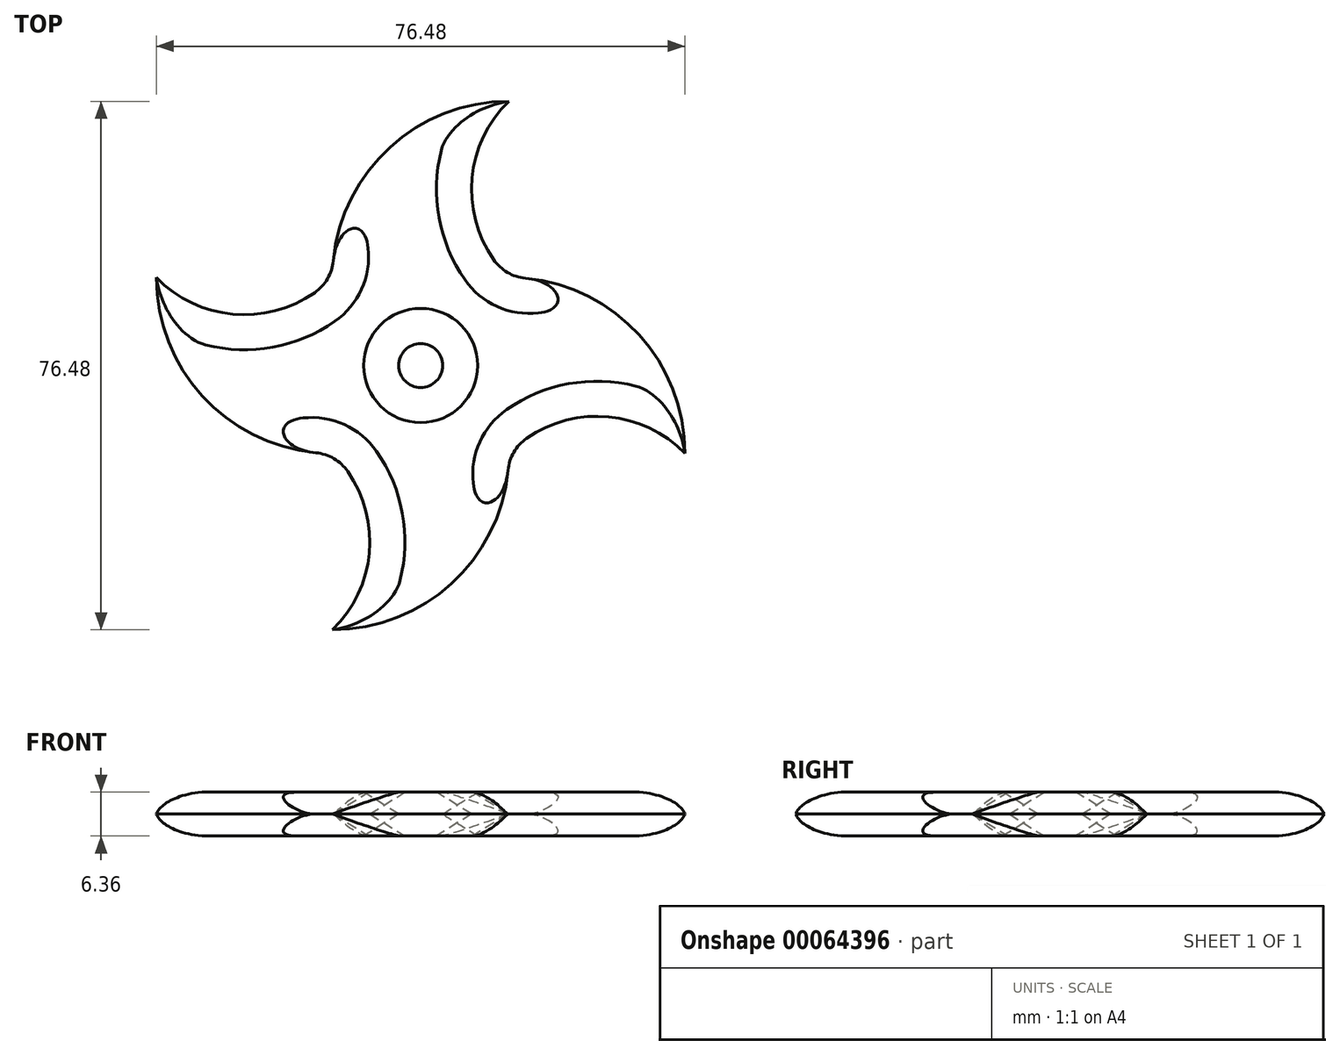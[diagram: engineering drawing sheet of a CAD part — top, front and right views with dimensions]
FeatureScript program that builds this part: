
annotation { "Feature Type Name" : "Feature", "Feature Type Description" : "" }
export const myFeature = defineFeature(function(context is Context, id is Id, definition is map)
    precondition{}
    {
        {
            var Q0;
            Q0=qCreatedBy(makeId("Top.planeOp"),FACE);
            var sketch = newSketch(context, id + "F0", { "sketchPlane" : qUnion([Q0])});
            skLineSegment(sketch, "E0.bottom", {"start": v(-12.75, 12.75) * mm, "end": v(12.74, 12.75) * mm});
            skLineSegment(sketch, "E0.top", {"start": v(-12.75, -12.74) * mm, "end": v(12.74, -12.74) * mm});
            skLineSegment(sketch, "E0.left", {"start": v(-12.75, 12.75) * mm, "end": v(-12.75, -12.74) * mm});
            skLineSegment(sketch, "E0.right", {"start": v(12.74, 12.75) * mm, "end": v(12.74, -12.74) * mm});
            skArc(sketch, "E1", {"start": v(-12.64, 15.16) * mm, "mid": v(-4.41, 31.6) * mm, "end": v(12.74, 38.24) * mm});
            skArc(sketch, "E2", {"start": v(12.74, 38.24) * mm, "mid": v(7.44, 27.18) * mm, "end": v(10.55, 15.33) * mm});
            skCircle(sketch, "E3", {"center": v(0, 0) * mm, "radius": 3.18 * mm});
            skArc(sketch, "E4.1.0", {"start": v(-38.24, 12.74) * mm, "mid": v(-27.18, 7.44) * mm, "end": v(-15.33, 10.55) * mm});
            skArc(sketch, "E4.1.1", {"start": v(-15.16, -12.64) * mm, "mid": v(-31.6, -4.41) * mm, "end": v(-38.24, 12.74) * mm});
            skLineSegment(sketch, "E4.1.2", {"start": v(-12.75, -12.75) * mm, "end": v(-12.75, 12.74) * mm});
            skArc(sketch, "E4.2.0", {"start": v(-12.74, -38.24) * mm, "mid": v(-7.44, -27.18) * mm, "end": v(-10.55, -15.33) * mm});
            skArc(sketch, "E4.2.1", {"start": v(12.64, -15.16) * mm, "mid": v(4.41, -31.6) * mm, "end": v(-12.74, -38.24) * mm});
            skLineSegment(sketch, "E4.2.2", {"start": v(12.75, -12.75) * mm, "end": v(-12.74, -12.75) * mm});
            skArc(sketch, "E4.3.0", {"start": v(38.24, -12.74) * mm, "mid": v(27.18, -7.44) * mm, "end": v(15.33, -10.55) * mm});
            skArc(sketch, "E4.3.1", {"start": v(15.16, 12.64) * mm, "mid": v(31.6, 4.41) * mm, "end": v(38.24, -12.74) * mm});
            skLineSegment(sketch, "E4.3.2", {"start": v(12.75, 12.75) * mm, "end": v(12.75, -12.74) * mm});
            skPoint(sketch, "E5.newPointB", {"position": v(-12.75, 12.75) * mm});
            skArc(sketch, "E5.filletArc", {"start": v(-15.33, 10.55) * mm, "mid": v(-13.47, 12.56) * mm, "end": v(-12.64, 15.16) * mm});
            skPoint(sketch, "E6.newPointB", {"position": v(12.75, 12.75) * mm});
            skArc(sketch, "E6.filletArc", {"start": v(10.55, 15.33) * mm, "mid": v(12.56, 13.47) * mm, "end": v(15.16, 12.64) * mm});
            skPoint(sketch, "E7.newPointB", {"position": v(12.75, -12.75) * mm});
            skArc(sketch, "E7.filletArc", {"start": v(15.33, -10.55) * mm, "mid": v(13.47, -12.56) * mm, "end": v(12.64, -15.16) * mm});
            skPoint(sketch, "E8.newPointB", {"position": v(-12.75, -12.75) * mm});
            skArc(sketch, "E8.filletArc", {"start": v(-10.55, -15.33) * mm, "mid": v(-12.56, -13.47) * mm, "end": v(-15.16, -12.64) * mm});
            skSolve(sketch);
        }
        {
            var Q0;
            Q0 = qSketchRegion(id + "F0", true);
            var Q1;
            Q1=makeQuery(id+"F0.imprint","IMPRINT",FACE,{"disambiguationData":[TD([[makeQuery(id+"F0.imprint","IMPRINT",EDGE,{"derivedFrom":sQuery(id+"F0.wireOp",EDGE,"E0.bottom")}),-1.0]])]});
            extrude(context, id + "F1", {"entities" : qUnion([Q0, Q1]), "depth" : 3.17 * mm});
        }
        {
            var Q0;
            Q0=makeQuery(id+"F1.opExtrude","CAP_EDGE",EDGE,{"disambiguationData":[OSD([sQuery(id+"F0.wireOp",EDGE,"E5.filletArc")])],"isStart":false});
            var Q1;
            Q1=makeQuery(id+"F1.opExtrude","CAP_EDGE",EDGE,{"disambiguationData":[OSD([sQuery(id+"F0.wireOp",EDGE,"E4.1.0")])],"isStart":false});
            var Q2;
            Q2=makeQuery(id+"F1.opExtrude","CAP_EDGE",EDGE,{"disambiguationData":[OSD([sQuery(id+"F0.wireOp",EDGE,"E8.filletArc")])],"isStart":false});
            var Q3;
            Q3=makeQuery(id+"F1.opExtrude","CAP_EDGE",EDGE,{"disambiguationData":[OSD([sQuery(id+"F0.wireOp",EDGE,"E4.2.0")])],"isStart":false});
            var Q4;
            Q4=makeQuery(id+"F1.opExtrude","CAP_EDGE",EDGE,{"disambiguationData":[OSD([sQuery(id+"F0.wireOp",EDGE,"E4.3.0")])],"isStart":false});
            var Q5;
            Q5=makeQuery(id+"F1.opExtrude","CAP_EDGE",EDGE,{"disambiguationData":[OSD([sQuery(id+"F0.wireOp",EDGE,"E6.filletArc")])],"isStart":false});
            var Q6;
            Q6=makeQuery(id+"F1.opExtrude","CAP_EDGE",EDGE,{"disambiguationData":[OSD([sQuery(id+"F0.wireOp",EDGE,"E2")])],"isStart":false});
            var Q7;
            Q7=makeQuery(id+"F1.opExtrude","CAP_EDGE",EDGE,{"disambiguationData":[OSD([sQuery(id+"F0.wireOp",EDGE,"E3")])],"isStart":false});
            var Q8;
            Q8=makeQuery(id+"F1.opExtrude","CAP_EDGE",EDGE,{"disambiguationData":[OSD([sQuery(id+"F0.wireOp",EDGE,"E7.filletArc")])],"isStart":false});
            chamfer(context, id + "F2", {"entities" : qUnion([Q0, Q1, Q2, Q3, Q4, Q5, Q6, Q7, Q8]), "chamferType" : ChamferType.TWO_OFFSETS, "width1" : 3.17 * mm, "oppositeDirection" : false, "width2" : 5.08 * mm});
        }
        {
            var Q0;
            Q0=makeQuery(id+"F1.opExtrude","CAP_EDGE",EDGE,{"disambiguationData":[OSD([sQuery(id+"F0.wireOp",EDGE,"E4.2.1")])],"isStart":false});
            var Q1;
            Q1=makeQuery(id+"F1.opExtrude","CAP_EDGE",EDGE,{"disambiguationData":[OSD([sQuery(id+"F0.wireOp",EDGE,"E4.3.1")])],"isStart":false});
            var Q2;
            Q2=makeQuery(id+"F1.opExtrude","CAP_EDGE",EDGE,{"disambiguationData":[OSD([sQuery(id+"F0.wireOp",EDGE,"E1")])],"isStart":false});
            var Q3;
            Q3=makeQuery(id+"F1.opExtrude","CAP_EDGE",EDGE,{"disambiguationData":[OSD([sQuery(id+"F0.wireOp",EDGE,"E4.1.1")])],"isStart":false});
            fillet(context, id + "F3", {"entities" : qUnion([Q0, Q1, Q2, Q3]), "radius" : 5.08 * mm, "tangentPropagation" : true, "allowEdgeOverflow" : false});
        }
        {
            var Q0;
            Q0=makeQuery(id+"F1.opExtrude","SWEPT_BODY",BODY,{"disambiguationData":[OSD([sQuery(id+"F0.wireOp",EDGE,"E1"),sQuery(id+"F0.wireOp",EDGE,"E2"),sQuery(id+"F0.wireOp",EDGE,"E3"),sQuery(id+"F0.wireOp",EDGE,"E4.1.0"),sQuery(id+"F0.wireOp",EDGE,"E4.1.1"),sQuery(id+"F0.wireOp",EDGE,"E4.2.0"),sQuery(id+"F0.wireOp",EDGE,"E4.2.1"),sQuery(id+"F0.wireOp",EDGE,"E4.3.0"),sQuery(id+"F0.wireOp",EDGE,"E4.3.1"),sQuery(id+"F0.wireOp",EDGE,"E5.filletArc"),sQuery(id+"F0.wireOp",EDGE,"E6.filletArc"),sQuery(id+"F0.wireOp",EDGE,"E7.filletArc"),sQuery(id+"F0.wireOp",EDGE,"E8.filletArc")])]});
            var Q1;
            Q1=makeQuery(id+"F1.opExtrude","CAP_FACE",FACE,{"disambiguationData":[OSD([sQuery(id+"F0.wireOp",EDGE,"E1"),sQuery(id+"F0.wireOp",EDGE,"E2"),sQuery(id+"F0.wireOp",EDGE,"E3"),sQuery(id+"F0.wireOp",EDGE,"E4.1.0"),sQuery(id+"F0.wireOp",EDGE,"E4.1.1"),sQuery(id+"F0.wireOp",EDGE,"E4.2.0"),sQuery(id+"F0.wireOp",EDGE,"E4.2.1"),sQuery(id+"F0.wireOp",EDGE,"E4.3.0"),sQuery(id+"F0.wireOp",EDGE,"E4.3.1"),sQuery(id+"F0.wireOp",EDGE,"E5.filletArc"),sQuery(id+"F0.wireOp",EDGE,"E6.filletArc"),sQuery(id+"F0.wireOp",EDGE,"E7.filletArc"),sQuery(id+"F0.wireOp",EDGE,"E8.filletArc")])],"isStart":true});
            mirror(context, id + "F4", {"operationType" : NewBodyOperationType.ADD, "entities" : qUnion([Q0]), "mirrorPlane" : qUnion([Q1])});
        }
    });
